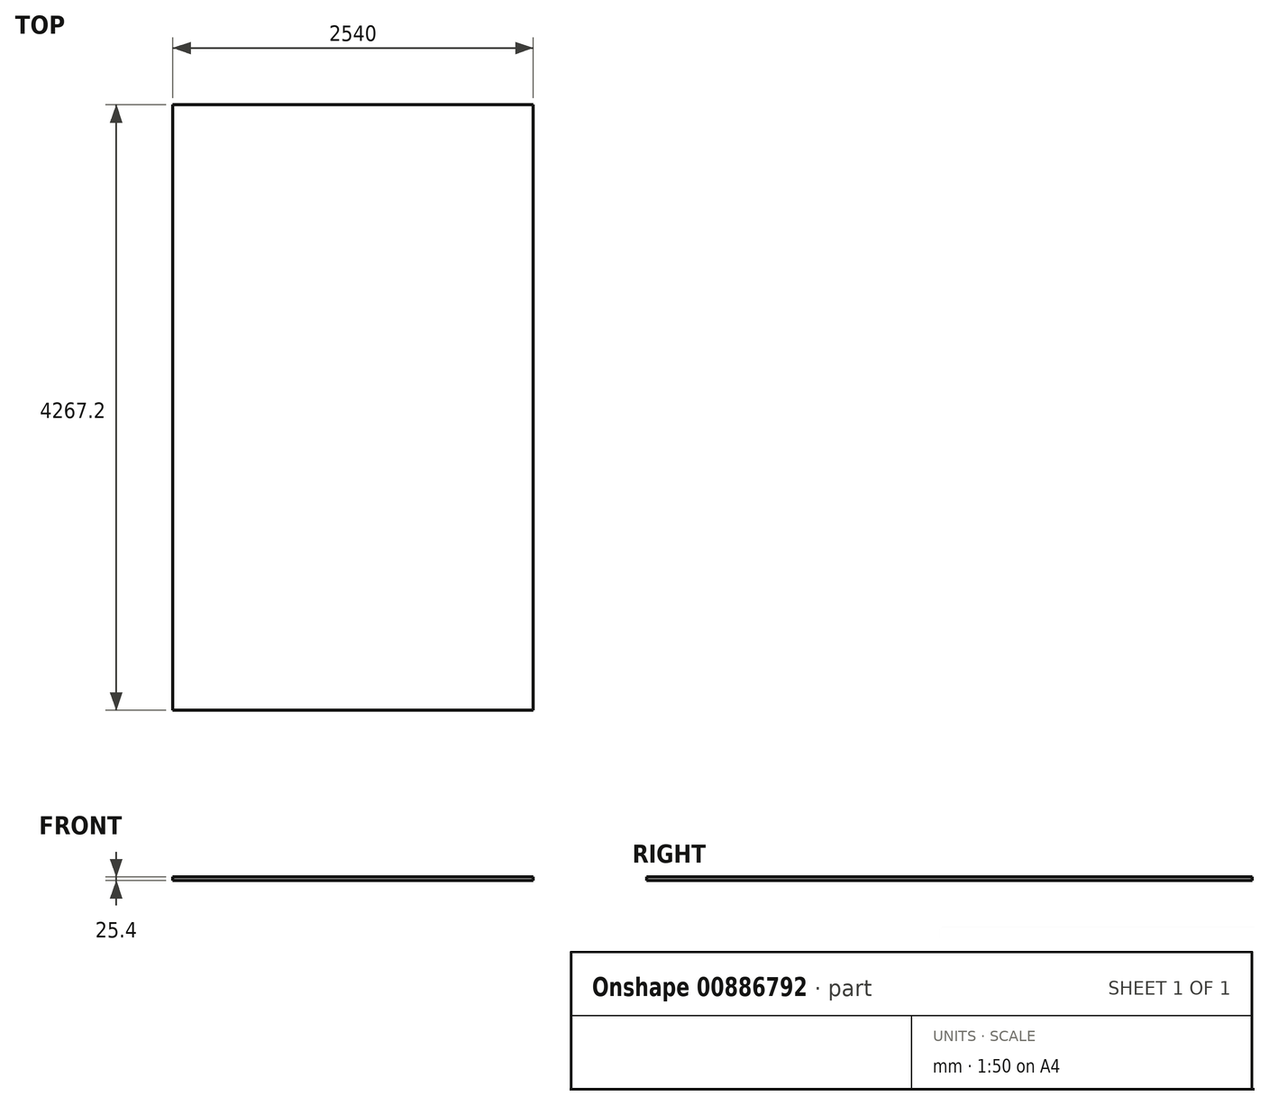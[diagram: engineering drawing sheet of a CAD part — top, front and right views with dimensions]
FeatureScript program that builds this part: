
annotation { "Feature Type Name" : "Feature", "Feature Type Description" : "" }
export const myFeature = defineFeature(function(context is Context, id is Id, definition is map)
    precondition{}
    {
        {
            var Q0;
            Q0=qCreatedBy(makeId("Top.planeOp"),FACE);
            var sketch = newSketch(context, id + "F0", { "sketchPlane" : qUnion([Q0])});
            skLineSegment(sketch, "E0.bottom", {"start": v(-1102.2, 2133.6) * mm, "end": v(1437.8, 2133.6) * mm});
            skLineSegment(sketch, "E0.top", {"start": v(-1102.2, -2133.6) * mm, "end": v(1437.8, -2133.6) * mm});
            skLineSegment(sketch, "E0.left", {"start": v(-1102.2, 2133.6) * mm, "end": v(-1102.2, -2133.6) * mm});
            skLineSegment(sketch, "E0.right", {"start": v(1437.8, 2133.6) * mm, "end": v(1437.8, -2133.6) * mm});
            skPoint(sketch, "E0.middle", {"position": v(167.8, 0) * mm});
            skSolve(sketch);
        }
        {
            var Q0;
            Q0 = qSketchRegion(id + "F0", true);
            extrude(context, id + "F1", {"entities" : qUnion([Q0]), "depth" : 25.4 * mm, "offsetDistance" : 25.4 * mm});
        }
    });
